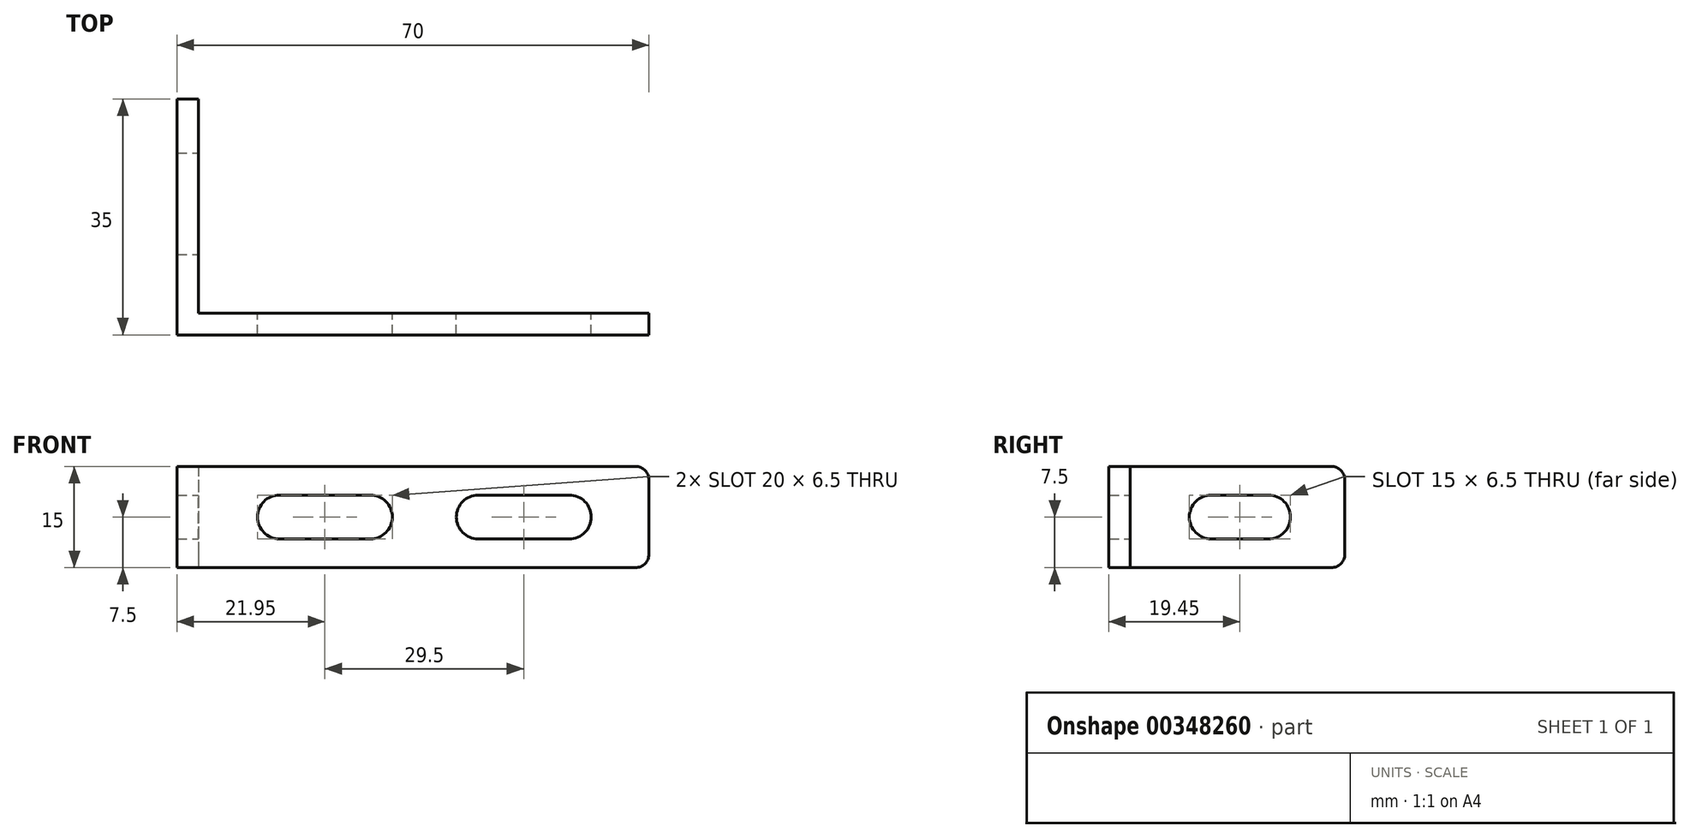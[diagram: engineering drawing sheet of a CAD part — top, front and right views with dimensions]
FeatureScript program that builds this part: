
annotation { "Feature Type Name" : "Feature", "Feature Type Description" : "" }
export const myFeature = defineFeature(function(context is Context, id is Id, definition is map)
    precondition{}
    {
        {
            var Q0;
            Q0=qCreatedBy(makeId("Top.planeOp"),FACE);
            var sketch = newSketch(context, id + "F0", { "sketchPlane" : qUnion([Q0])});
            skLineSegment(sketch, "E0", {"start": v(0, 35) * mm, "end": v(0, 0) * mm});
            skLineSegment(sketch, "E1", {"start": v(0, 0) * mm, "end": v(70, 0) * mm});
            skLineSegment(sketch, "E2", {"start": v(70, 0) * mm, "end": v(70, 3.2) * mm});
            skLineSegment(sketch, "E3", {"start": v(70, 3.2) * mm, "end": v(3.2, 3.2) * mm});
            skLineSegment(sketch, "E4", {"start": v(3.2, 3.2) * mm, "end": v(3.2, 35) * mm});
            skLineSegment(sketch, "E5", {"start": v(3.2, 35) * mm, "end": v(0, 35) * mm});
            skSolve(sketch);
        }
        {
            var Q0;
            Q0=makeQuery(id+"F0.imprint","IMPRINT",FACE,{"disambiguationData":[TD([[makeQuery(id+"F0.imprint","IMPRINT",EDGE,{"derivedFrom":sQuery(id+"F0.wireOp",EDGE,"E0")}),1.0]])]});
            extrude(context, id + "F1", {"entities" : qUnion([Q0]), "depth" : 15 * mm});
        }
        {
            var Q0;
            Q0=makeQuery(id+"F1.opExtrude","SWEPT_FACE",FACE,{"disambiguationData":[OSD([sQuery(id+"F0.wireOp",EDGE,"E3")])]});
            var sketch = newSketch(context, id + "F2", { "sketchPlane" : qUnion([Q0])});
            skArc(sketch, "E6", {"start": v(-28.7, 10.75) * mm, "mid": v(-31.95, 7.5) * mm, "end": v(-28.7, 4.25) * mm});
            skArc(sketch, "E7", {"start": v(-15.2, 4.25) * mm, "mid": v(-11.95, 7.5) * mm, "end": v(-15.2, 10.75) * mm});
            skLineSegment(sketch, "E8", {"start": v(-28.7, 10.75) * mm, "end": v(-15.2, 10.75) * mm});
            skLineSegment(sketch, "E9", {"start": v(-28.7, 4.25) * mm, "end": v(-15.2, 4.25) * mm});
            skArc(sketch, "E10", {"start": v(-44.7, 4.25) * mm, "mid": v(-41.45, 7.5) * mm, "end": v(-44.7, 10.75) * mm});
            skLineSegment(sketch, "E11", {"start": v(-58.2, 10.75) * mm, "end": v(-44.7, 10.75) * mm});
            skLineSegment(sketch, "E12", {"start": v(-44.7, 4.25) * mm, "end": v(-58.2, 4.25) * mm});
            skArc(sketch, "E13", {"start": v(-58.2, 10.75) * mm, "mid": v(-61.45, 7.5) * mm, "end": v(-58.2, 4.25) * mm});
            skSolve(sketch);
        }
        {
            var Q0;
            Q0=makeQuery(id+"F1.opExtrude","SWEPT_FACE",FACE,{"disambiguationData":[OSD([sQuery(id+"F0.wireOp",EDGE,"E4")])]});
            var sketch = newSketch(context, id + "F3", { "sketchPlane" : qUnion([Q0])});
            skArc(sketch, "E14", {"start": v(15.2, 10.75) * mm, "mid": v(11.95, 7.5) * mm, "end": v(15.2, 4.25) * mm});
            skPoint(sketch, "E14.centerSnap0", {"position": v(3.2, 7.5) * mm});
            skArc(sketch, "E15", {"start": v(23.7, 4.25) * mm, "mid": v(26.95, 7.5) * mm, "end": v(23.7, 10.75) * mm});
            skLineSegment(sketch, "E16", {"start": v(15.2, 10.75) * mm, "end": v(23.7, 10.75) * mm});
            skLineSegment(sketch, "E17", {"start": v(23.7, 4.25) * mm, "end": v(15.2, 4.25) * mm});
            skSolve(sketch);
        }
        {
            var Q0;
            Q0=makeQuery(id+"F2.imprint","IMPRINT",FACE,{"disambiguationData":[TD([[makeQuery(id+"F2.imprint","IMPRINT",EDGE,{"derivedFrom":sQuery(id+"F2.wireOp",EDGE,"E6")}),1.0]])]});
            var Q1;
            Q1=makeQuery(id+"F2.imprint","IMPRINT",FACE,{"disambiguationData":[TD([[makeQuery(id+"F2.imprint","IMPRINT",EDGE,{"derivedFrom":sQuery(id+"F2.wireOp",EDGE,"E10")}),1.0]])]});
            extrude(context, id + "F4", {"entities" : qUnion([Q0, Q1]), "operationType" : NewBodyOperationType.REMOVE, "endBound" : BoundingType.THROUGH_ALL, "oppositeDirection" : true, "depth" : 25 * mm});
        }
        {
            var Q0;
            Q0=makeQuery(id+"F3.imprint","IMPRINT",FACE,{"disambiguationData":[TD([[makeQuery(id+"F3.imprint","IMPRINT",EDGE,{"derivedFrom":sQuery(id+"F3.wireOp",EDGE,"E14")}),1.0]])]});
            extrude(context, id + "F5", {"entities" : qUnion([Q0]), "operationType" : NewBodyOperationType.REMOVE, "endBound" : BoundingType.THROUGH_ALL, "oppositeDirection" : true, "depth" : 25 * mm});
        }
        {
            var Q0;
            Q0=makeQuery(id+"F1.opExtrude","CAP_EDGE",EDGE,{"disambiguationData":[OSD([sQuery(id+"F0.wireOp",EDGE,"E2")])],"isStart":false});
            var Q1;
            Q1=makeQuery(id+"F1.opExtrude","CAP_EDGE",EDGE,{"disambiguationData":[OSD([sQuery(id+"F0.wireOp",EDGE,"E2")])],"isStart":true});
            var Q2;
            Q2=makeQuery(id+"F1.opExtrude","CAP_EDGE",EDGE,{"disambiguationData":[OSD([sQuery(id+"F0.wireOp",EDGE,"E5")])],"isStart":false});
            var Q3;
            Q3=makeQuery(id+"F1.opExtrude","CAP_EDGE",EDGE,{"disambiguationData":[OSD([sQuery(id+"F0.wireOp",EDGE,"E5")])],"isStart":true});
            fillet(context, id + "F6", {"entities" : qUnion([Q0, Q1, Q2, Q3]), "radius" : 2 * mm, "tangentPropagation" : true, "allowEdgeOverflow" : false});
        }
    });
